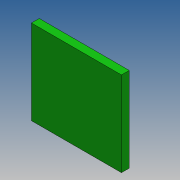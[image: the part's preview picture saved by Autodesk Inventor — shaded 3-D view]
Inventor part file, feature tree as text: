
AUTODESK INVENTOR PART (.ipt)
format: ipt  version: 2017 (Build 210142000, 142)  size: 805,888 bytes
history: native  units: mm
features: other x11, extrude x1, sketch x1
ambient origin geometry x8: Origin, YZ Plane, XZ Plane, XY Plane, X Axis, Y Axis, Z Axis, Center Point
bodies: Body1 (feature_tree), Body2 (feature_tree), Body3 (feature_tree)
feature tree (13):
  other  "MINIUSBSHELL.ipt"
  other  "MINIUSBCORE.ipt"
  other  "Desplazar cuerpo1"
  other  "Desplazar cuerpo2"
  extrude  "Extrusión1"  Depth=10.0mm
  other  "Solid1::MINIUSBSHELL.ipt"
  other  "OperaciónIdentificador1"
  other  "Solid1::MINIUSBCORE.ipt"
  other  "OperaciónIdentificador2"
  sketch  "Boceto1"  dims[d0=10.0mm d1=10.0mm d2=180.0deg d3=0.0mm d4=0.0mm d5=7.0mm d6=1.5mm d7=0.0mm]
  other  "Sólido3"
  other  "Sólido1"
  other  "Sólido2"
